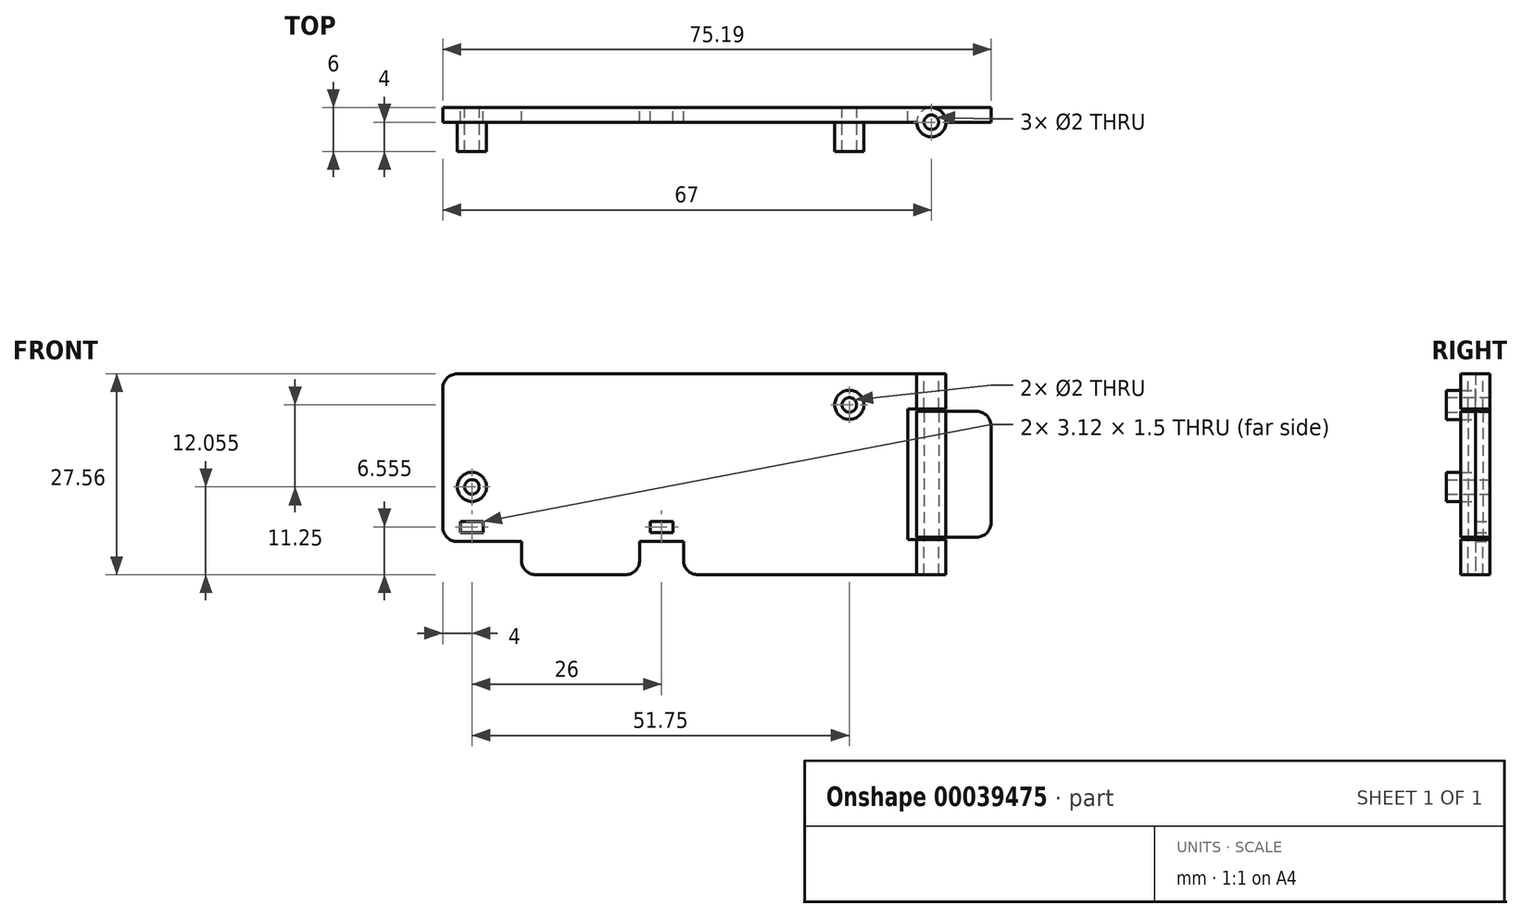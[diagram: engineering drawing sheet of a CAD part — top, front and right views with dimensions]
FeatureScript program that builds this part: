
annotation { "Feature Type Name" : "Feature", "Feature Type Description" : "" }
export const myFeature = defineFeature(function(context is Context, id is Id, definition is map)
    precondition{}
    {
        {
            var Q0;
            Q0=qCreatedBy(makeId("Front.planeOp"),FACE);
            var sketch = newSketch(context, id + "F0", { "sketchPlane" : qUnion([Q0])});
            skLineSegment(sketch, "E0.rect.bottom", {"start": v(33.5, -13.77) * mm, "end": v(-33.5, -13.78) * mm});
            skLineSegment(sketch, "E0.rect.top", {"start": v(33.5, 13.78) * mm, "end": v(-33.5, 13.77) * mm});
            skLineSegment(sketch, "E0.rect.left", {"start": v(33.5, -13.77) * mm, "end": v(33.5, 13.78) * mm});
            skLineSegment(sketch, "E0.rect.right", {"start": v(-33.5, -13.78) * mm, "end": v(-33.5, 13.77) * mm});
            skPoint(sketch, "E0.rect.middle", {"position": v(0, 0) * mm});
            skLineSegment(sketch, "E1.top", {"start": v(-33.5, -7.23) * mm, "end": v(24.5, -7.22) * mm});
            skLineSegment(sketch, "E1.right", {"start": v(24.5, 13.78) * mm, "end": v(24.5, -7.22) * mm});
            skCircle(sketch, "E2", {"center": v(-29.5, -1.73) * mm, "radius": 1 * mm});
            skCircle(sketch, "E3", {"center": v(22.25, 9.53) * mm, "radius": 1 * mm});
            skLineSegment(sketch, "E4.bottom", {"start": v(-6.5, -9.23) * mm, "end": v(-0.5, -9.23) * mm});
            skLineSegment(sketch, "E4.top", {"start": v(-6.5, -13.78) * mm, "end": v(-0.5, -13.78) * mm});
            skLineSegment(sketch, "E4.left", {"start": v(-6.5, -9.23) * mm, "end": v(-6.5, -13.78) * mm});
            skLineSegment(sketch, "E4.right", {"start": v(-0.5, -9.23) * mm, "end": v(-0.5, -13.78) * mm});
            skLineSegment(sketch, "E5.bottom", {"start": v(-33.5, -9.23) * mm, "end": v(-22.71, -9.23) * mm});
            skLineSegment(sketch, "E5.top", {"start": v(-33.5, -13.78) * mm, "end": v(-22.71, -13.78) * mm});
            skLineSegment(sketch, "E5.left", {"start": v(-33.5, -9.23) * mm, "end": v(-33.5, -13.78) * mm});
            skLineSegment(sketch, "E5.right", {"start": v(-22.71, -9.23) * mm, "end": v(-22.71, -13.78) * mm});
            skCircle(sketch, "E6.0", {"center": v(22.25, 9.53) * mm, "radius": 2 * mm});
            skCircle(sketch, "E7.0", {"center": v(-29.5, -1.73) * mm, "radius": 2 * mm});
            skLineSegment(sketch, "E8", {"start": v(-22.71, -11.5) * mm, "end": v(-42.23, -11.5) * mm, "construction": true});
            skLineSegment(sketch, "E9.rect.bottom", {"start": v(-27.94, -7.98) * mm, "end": v(-31.06, -7.98) * mm});
            skLineSegment(sketch, "E9.rect.top", {"start": v(-27.94, -6.47) * mm, "end": v(-31.06, -6.47) * mm});
            skLineSegment(sketch, "E9.rect.left", {"start": v(-27.94, -7.98) * mm, "end": v(-27.94, -6.47) * mm});
            skLineSegment(sketch, "E9.rect.right", {"start": v(-31.06, -7.98) * mm, "end": v(-31.06, -6.47) * mm});
            skPoint(sketch, "E9.rect.middle", {"position": v(-29.5, -7.23) * mm});
            skLineSegment(sketch, "E10.rect.bottom", {"start": v(-5.06, -7.98) * mm, "end": v(-1.94, -7.98) * mm});
            skLineSegment(sketch, "E10.rect.top", {"start": v(-5.06, -6.47) * mm, "end": v(-1.94, -6.47) * mm});
            skLineSegment(sketch, "E10.rect.left", {"start": v(-5.06, -7.98) * mm, "end": v(-5.06, -6.47) * mm});
            skLineSegment(sketch, "E10.rect.right", {"start": v(-1.94, -7.98) * mm, "end": v(-1.94, -6.47) * mm});
            skPoint(sketch, "E10.rect.middle", {"position": v(-3.5, -7.23) * mm});
            skPoint(sketch, "E10.rect.middle.positionSnap0", {"position": v(-3.5, -9.23) * mm});
            skPoint(sketch, "E10.rect.centerSnap0", {"position": v(-3.5, -9.23) * mm});
            skLineSegment(sketch, "E11", {"start": v(24.5, -7.22) * mm, "end": v(33.5, -7.22) * mm});
            skLineSegment(sketch, "E12", {"start": v(24.5, -7.22) * mm, "end": v(24.5, -13.77) * mm});
            skSolve(sketch);
        }
        {
            var Q0;
            {var subQ3=sQuery(id+"F0.wireOp",EDGE,"E0.rect.bottom");Q0=makeQuery(id+"F0.imprint","IMPRINT",FACE,{"disambiguationData":[TD([[makeQuery(id+"F0.imprint","IMPRINT",EDGE,{"derivedFrom":subQ3}),-1.0]])]});}
            var Q1;
            {var subQ4=sQuery(id+"F0.wireOp",EDGE,"E1.top");Q1=makeQuery(id+"F0.imprint","IMPRINT",FACE,{"disambiguationData":[TD([[makeQuery(id+"F0.imprint","IMPRINT",EDGE,{"derivedFrom":subQ4}),1.0]])]});}
            var Q2;
            {var subQ0=sQuery(id+"F0.wireOp",EDGE,"E1.right");Q2=makeQuery(id+"F0.imprint","IMPRINT",FACE,{"disambiguationData":[TD([[makeQuery(id+"F0.imprint","IMPRINT",EDGE,{"derivedFrom":subQ0}),1.0]])]});}
            var Q3;
            Q3=makeQuery(id+"F0.imprint","IMPRINT",FACE,{"disambiguationData":[TD([[makeQuery(id+"F0.imprint","IMPRINT",EDGE,{"derivedFrom":sQuery(id+"F0.wireOp",EDGE,"E3")}),-1.0]])]});
            var Q4;
            Q4=makeQuery(id+"F0.imprint","IMPRINT",FACE,{"disambiguationData":[TD([[makeQuery(id+"F0.imprint","IMPRINT",EDGE,{"derivedFrom":sQuery(id+"F0.wireOp",EDGE,"E2")}),-1.0]])]});
            var Q5;
            {var subQ2=sQuery(id+"F0.wireOp",EDGE,"E11");Q5=makeQuery(id+"F0.imprint","IMPRINT",FACE,{"disambiguationData":[TD([[makeQuery(id+"F0.imprint","IMPRINT",EDGE,{"derivedFrom":subQ2}),-1.0]])]});}
            extrude(context, id + "F1", {"entities" : qUnion([Q0, Q1, Q2, Q3, Q4, Q5]), "depth" : 2 * mm});
        }
        {
            var Q0;
            Q0=makeQuery(id+"F0.imprint","IMPRINT",FACE,{"disambiguationData":[TD([[makeQuery(id+"F0.imprint","IMPRINT",EDGE,{"derivedFrom":sQuery(id+"F0.wireOp",EDGE,"E2")}),-1.0]])]});
            var Q1;
            Q1=makeQuery(id+"F0.imprint","IMPRINT",FACE,{"disambiguationData":[TD([[makeQuery(id+"F0.imprint","IMPRINT",EDGE,{"derivedFrom":sQuery(id+"F0.wireOp",EDGE,"E3")}),-1.0]])]});
            extrude(context, id + "F2", {"entities" : qUnion([Q0, Q1]), "operationType" : NewBodyOperationType.ADD, "depth" : 6 * mm});
        }
        {
            var Q0;
            Q0=qCreatedBy(makeId("Top.planeOp"),FACE);
            var sketch = newSketch(context, id + "F3", { "sketchPlane" : qUnion([Q0])});
            skLineSegment(sketch, "E13.0.1", {"start": v(-33.5, 0) * mm, "end": v(-33.5, -2) * mm, "construction": true});
            skLineSegment(sketch, "E13.0.2", {"start": v(-33.5, -2) * mm, "end": v(33.5, -2) * mm, "construction": true});
            skLineSegment(sketch, "E14.0", {"start": v(33.5, 0) * mm, "end": v(-33.5, 0) * mm});
            skCircle(sketch, "E15", {"center": v(33.5, -2) * mm, "radius": 2 * mm});
            skCircle(sketch, "E16", {"center": v(33.5, -2) * mm, "radius": 1 * mm});
            skSolve(sketch);
        }
        {
            var Q0;
            Q0=makeQuery(id+"F3.imprint","IMPRINT",FACE,{"disambiguationData":[TD([[makeQuery(id+"F3.imprint","IMPRINT",EDGE,{"derivedFrom":sQuery(id+"F3.wireOp",EDGE,"E15")}),1.0]])]});
            var Q1;
            Q1=makeQuery(id+"F3.imprint","IMPRINT",FACE,{"disambiguationData":[TD([[makeQuery(id+"F3.imprint","IMPRINT",EDGE,{"derivedFrom":sQuery(id+"F3.wireOp",EDGE,"E16")}),1.0]])]});
            var Q2;
            Q2=makeQuery(id+"F1.opExtrude","SWEPT_FACE",FACE,{"disambiguationData":[OSD([sQuery(id+"F0.wireOp",EDGE,"E0.rect.top")])]});
            var Q3;
            {var subQ0=sQuery(id+"F0.wireOp",EDGE,"E0.rect.bottom");var subQ1=makeQuery(id+"F0.imprint","INTERSECT",VERTEX,{"derivedFrom":[subQ0,sQuery(id+"F0.wireOp",EDGE,"E12")]});Q3=makeQuery(id+"F1.opExtrude","SWEPT_FACE",FACE,{"disambiguationData":[OSD([subQ0]),TDD([makeQuery(id+"F0.imprint","IMPRINT",EDGE,{"disambiguationData":[TD([[makeQuery(id+"F0.imprint","INTERSECT",VERTEX,{"derivedFrom":[subQ0,sQuery(id+"F0.wireOp",EDGE,"E0.rect.left")]}),-1.0]])],"derivedFrom":subQ0}),makeQuery(id+"F0.imprint","IMPRINT",EDGE,{"disambiguationData":[TD([[subQ1,-1.0]])],"derivedFrom":subQ0})])]});}
            extrude(context, id + "F4", {"entities" : qUnion([Q0, Q1]), "operationType" : NewBodyOperationType.ADD, "endBound" : BoundingType.UP_TO_SURFACE, "endBoundEntityFace" : qUnion([Q2]), "depth" : 3.53 * mm, "hasSecondDirection" : true, "secondDirectionBound" : SecondDirectionBoundingType.UP_TO_SURFACE, "secondDirectionOppositeDirection" : true, "secondDirectionBoundEntityFace" : qUnion([Q3]), "secondDirectionDepth" : 10 * mm});
        }
        {
            var Q0;
            Q0=qCreatedBy(makeId("Front.planeOp"),FACE);
            var sketch = newSketch(context, id + "F5", { "sketchPlane" : qUnion([Q0])});
            skLineSegment(sketch, "E17.0", {"start": v(31.5, -13.77) * mm, "end": v(-0.5, -13.78) * mm});
            skLineSegment(sketch, "E17.1", {"start": v(35.5, -13.78) * mm, "end": v(31.5, -13.78) * mm});
            skLineSegment(sketch, "E17.2", {"start": v(35.5, 13.78) * mm, "end": v(31.5, 13.78) * mm});
            skLineSegment(sketch, "E17.3", {"start": v(31.5, 13.78) * mm, "end": v(-33.5, 13.77) * mm});
            skLineSegment(sketch, "E17.4.1", {"start": v(31.5, -13.78) * mm, "end": v(35.5, -13.78) * mm});
            skLineSegment(sketch, "E17.4.3", {"start": v(35.5, 13.78) * mm, "end": v(31.5, 13.78) * mm});
            skLineSegment(sketch, "E18.rect.bottom", {"start": v(40.73, -8.98) * mm, "end": v(30.27, -8.98) * mm});
            skLineSegment(sketch, "E18.rect.top", {"start": v(40.73, 8.98) * mm, "end": v(30.27, 8.98) * mm});
            skLineSegment(sketch, "E18.rect.left", {"start": v(40.73, -8.98) * mm, "end": v(40.73, 8.98) * mm});
            skLineSegment(sketch, "E18.rect.right", {"start": v(30.27, -8.98) * mm, "end": v(30.27, 8.98) * mm});
            skPoint(sketch, "E18.rect.middle", {"position": v(35.5, 0) * mm});
            skSolve(sketch);
        }
        {
            var Q0;
            Q0=makeQuery(id+"F5.imprint","IMPRINT",FACE,{"disambiguationData":[TD([[makeQuery(id+"F5.imprint","IMPRINT",EDGE,{"derivedFrom":sQuery(id+"F5.wireOp",EDGE,"E18.rect.bottom")}),-1.0]])]});
            extrude(context, id + "F6", {"entities" : qUnion([Q0]), "operationType" : NewBodyOperationType.REMOVE, "depth" : 6 * mm});
        }
        {
            var Q0;
            Q0=makeQuery(id+"F3.imprint","IMPRINT",FACE,{"disambiguationData":[TD([[makeQuery(id+"F3.imprint","IMPRINT",EDGE,{"derivedFrom":sQuery(id+"F3.wireOp",EDGE,"E15")}),1.0]])]});
            extrude(context, id + "F7", {"entities" : qUnion([Q0]), "endBound" : BoundingType.SYMMETRIC, "depth" : 17.25 * mm});
        }
        {
            var Q0;
            Q0=qCreatedBy(makeId("Front.planeOp"),FACE);
            var sketch = newSketch(context, id + "F8", { "sketchPlane" : qUnion([Q0])});
            skLineSegment(sketch, "E19.0", {"start": v(31.5, 8.62) * mm, "end": v(35.5, 8.62) * mm});
            skLineSegment(sketch, "E19.2", {"start": v(31.5, -8.62) * mm, "end": v(35.5, -8.62) * mm});
            skLineSegment(sketch, "E20.bottom", {"start": v(31.5, 8.62) * mm, "end": v(41.69, 8.62) * mm});
            skLineSegment(sketch, "E20.top", {"start": v(31.5, -8.62) * mm, "end": v(41.69, -8.62) * mm});
            skLineSegment(sketch, "E20.left", {"start": v(31.5, 8.62) * mm, "end": v(31.5, -8.62) * mm});
            skLineSegment(sketch, "E20.right", {"start": v(41.69, 8.62) * mm, "end": v(41.69, -8.62) * mm});
            skLineSegment(sketch, "E21.0", {"start": v(33.5, 8.98) * mm, "end": v(33.5, 13.78) * mm});
            skLineSegment(sketch, "E22", {"start": v(33.5, 8.98) * mm, "end": v(33.5, -10.13) * mm});
            skPoint(sketch, "E22.endSnap0", {"position": v(33.5, -8.62) * mm});
            skSolve(sketch);
        }
        {
            var Q0;
            {var subQ0=sQuery(id+"F8.wireOp",EDGE,"E20.right");Q0=makeQuery(id+"F8.imprint","IMPRINT",FACE,{"disambiguationData":[TD([[makeQuery(id+"F8.imprint","IMPRINT",EDGE,{"derivedFrom":subQ0}),-1.0]])]});}
            var Q1;
            Q1=makeQuery(id+"F1.opExtrude","CAP_FACE",FACE,{"disambiguationData":[OSD([sQuery(id+"F0.wireOp",EDGE,"E0.rect.bottom"),sQuery(id+"F0.wireOp",EDGE,"E0.rect.top"),sQuery(id+"F0.wireOp",EDGE,"E0.rect.left"),sQuery(id+"F0.wireOp",EDGE,"E0.rect.right"),sQuery(id+"F0.wireOp",EDGE,"E2"),sQuery(id+"F0.wireOp",EDGE,"E3"),sQuery(id+"F0.wireOp",EDGE,"E4.bottom"),sQuery(id+"F0.wireOp",EDGE,"E4.left"),sQuery(id+"F0.wireOp",EDGE,"E4.right"),sQuery(id+"F0.wireOp",EDGE,"E5.bottom"),sQuery(id+"F0.wireOp",EDGE,"E5.right"),sQuery(id+"F0.wireOp",EDGE,"E9.rect.bottom"),sQuery(id+"F0.wireOp",EDGE,"E9.rect.top"),sQuery(id+"F0.wireOp",EDGE,"E9.rect.left"),sQuery(id+"F0.wireOp",EDGE,"E9.rect.right"),sQuery(id+"F0.wireOp",EDGE,"E10.rect.bottom"),sQuery(id+"F0.wireOp",EDGE,"E10.rect.top"),sQuery(id+"F0.wireOp",EDGE,"E10.rect.left"),sQuery(id+"F0.wireOp",EDGE,"E10.rect.right")])],"isStart":false});
            extrude(context, id + "F9", {"entities" : qUnion([Q0]), "operationType" : NewBodyOperationType.ADD, "endBound" : BoundingType.UP_TO_SURFACE, "endBoundEntityFace" : qUnion([Q1]), "depth" : 25 * mm});
        }
        {
            var Q0;
            Q0=makeQuery(id+"F3.imprint","IMPRINT",FACE,{"disambiguationData":[TD([[makeQuery(id+"F3.imprint","IMPRINT",EDGE,{"derivedFrom":sQuery(id+"F3.wireOp",EDGE,"E16")}),1.0]])]});
            extrude(context, id + "F10", {"entities" : qUnion([Q0]), "operationType" : NewBodyOperationType.REMOVE, "endBound" : BoundingType.THROUGH_ALL, "oppositeDirection" : true, "depth" : 25 * mm, "hasSecondDirection" : true, "secondDirectionBound" : SecondDirectionBoundingType.THROUGH_ALL, "secondDirectionOppositeDirection" : false, "secondDirectionDepth" : 25 * mm});
        }
        {
            var Q0;
            Q0=makeQuery(id+"F1.opExtrude","SWEPT_EDGE",EDGE,{"disambiguationData":[OSD([sQuery(id+"F0.wireOp",EDGE,"E0.rect.right"),sQuery(id+"F0.wireOp",EDGE,"E5.bottom"),sQuery(id+"F0.wireOp",EDGE,"E5.left")])]});
            var Q1;
            Q1=makeQuery(id+"F1.opExtrude","SWEPT_EDGE",EDGE,{"disambiguationData":[OSD([sQuery(id+"F0.wireOp",EDGE,"E0.rect.top"),sQuery(id+"F0.wireOp",EDGE,"E0.rect.right")])]});
            var Q2;
            Q2=makeQuery(id+"F1.opExtrude","SWEPT_EDGE",EDGE,{"disambiguationData":[OSD([sQuery(id+"F0.wireOp",EDGE,"E0.rect.bottom"),sQuery(id+"F0.wireOp",EDGE,"E5.top"),sQuery(id+"F0.wireOp",EDGE,"E5.right")])]});
            var Q3;
            Q3=makeQuery(id+"F1.opExtrude","SWEPT_EDGE",EDGE,{"disambiguationData":[OSD([sQuery(id+"F0.wireOp",EDGE,"E0.rect.bottom"),sQuery(id+"F0.wireOp",EDGE,"E4.top"),sQuery(id+"F0.wireOp",EDGE,"E4.left")])]});
            var Q4;
            Q4=makeQuery(id+"F1.opExtrude","SWEPT_EDGE",EDGE,{"disambiguationData":[OSD([sQuery(id+"F0.wireOp",EDGE,"E0.rect.bottom"),sQuery(id+"F0.wireOp",EDGE,"E4.top"),sQuery(id+"F0.wireOp",EDGE,"E4.right")])]});
            var Q5;
            Q5=makeQuery(id+"F9.opExtrude","SWEPT_EDGE",EDGE,{"disambiguationData":[OSD([sQuery(id+"F8.wireOp",EDGE,"E20.top"),sQuery(id+"F8.wireOp",EDGE,"E20.right")])]});
            var Q6;
            Q6=makeQuery(id+"F9.opExtrude","SWEPT_EDGE",EDGE,{"disambiguationData":[OSD([sQuery(id+"F8.wireOp",EDGE,"E20.bottom"),sQuery(id+"F8.wireOp",EDGE,"E20.right")])]});
            fillet(context, id + "F11", {"entities" : qUnion([Q0, Q1, Q2, Q3, Q4, Q5, Q6]), "radius" : 2 * mm, "tangentPropagation" : true, "allowEdgeOverflow" : false});
        }
    });
